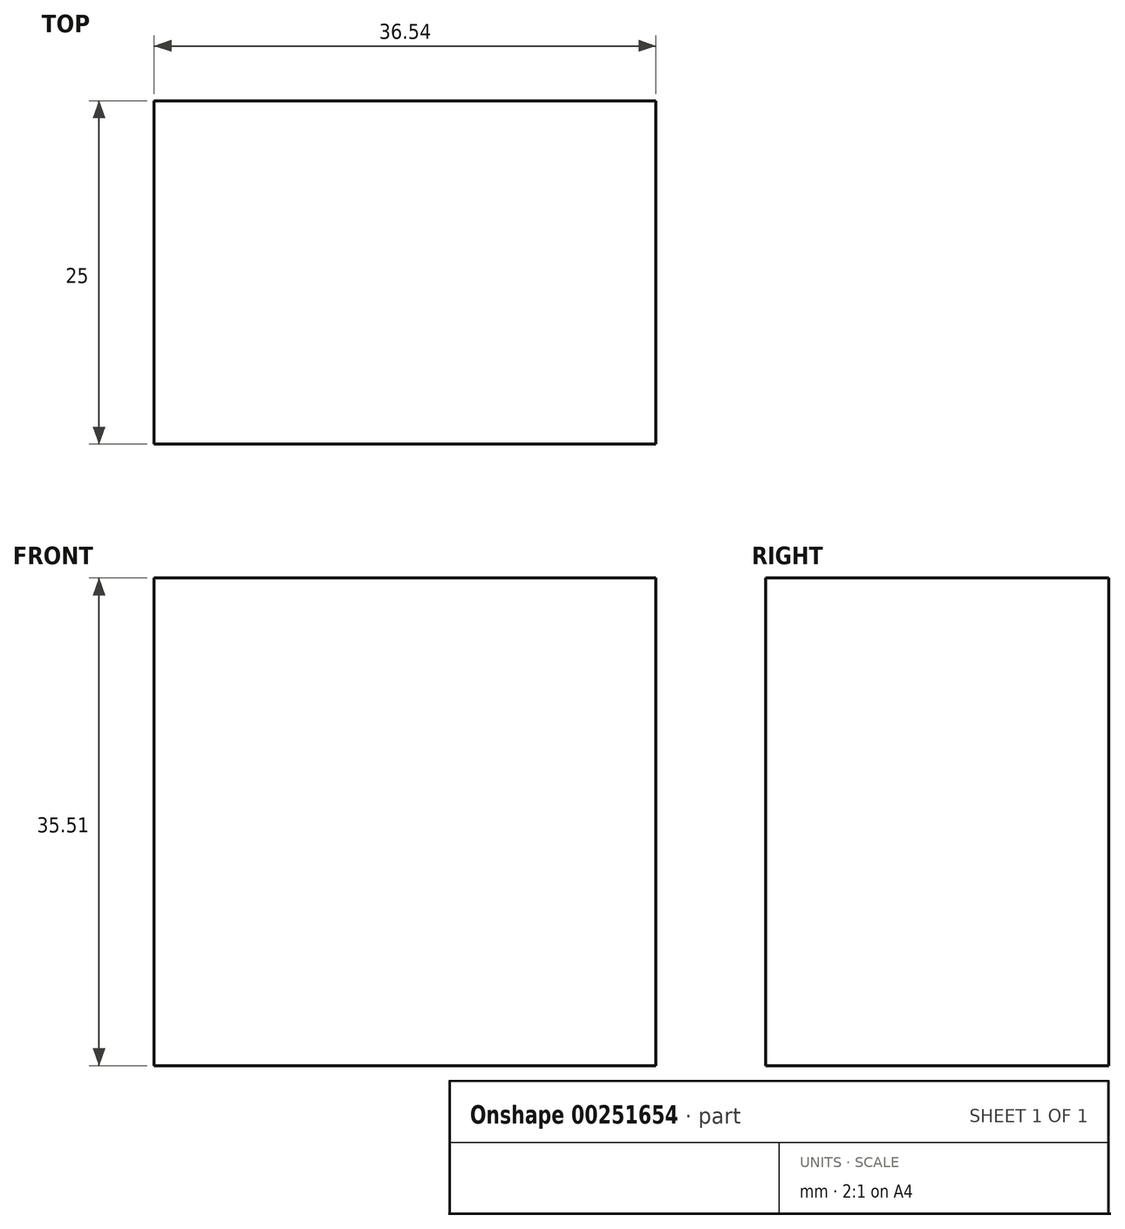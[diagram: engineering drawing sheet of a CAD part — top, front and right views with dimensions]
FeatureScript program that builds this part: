
annotation { "Feature Type Name" : "Feature", "Feature Type Description" : "" }
export const myFeature = defineFeature(function(context is Context, id is Id, definition is map)
    precondition{}
    {
        {
            var Q0;
            Q0=qCreatedBy(makeId("Front.planeOp"),FACE);
            var sketch = newSketch(context, id + "F0", { "sketchPlane" : qUnion([Q0])});
            skLineSegment(sketch, "E0.bottom", {"start": v(0, 0) * mm, "end": v(36.54, 0) * mm});
            skLineSegment(sketch, "E0.top", {"start": v(0, 35.5) * mm, "end": v(36.54, 35.5) * mm});
            skLineSegment(sketch, "E0.left", {"start": v(0, 0) * mm, "end": v(0, 35.5) * mm});
            skLineSegment(sketch, "E0.right", {"start": v(36.54, 0) * mm, "end": v(36.54, 35.5) * mm});
            skSolve(sketch);
        }
        {
            var Q0;
            Q0 = qSketchRegion(id + "F0", true);
            extrude(context, id + "F1", {"entities" : qUnion([Q0]), "depth" : 25 * mm});
        }
    });
